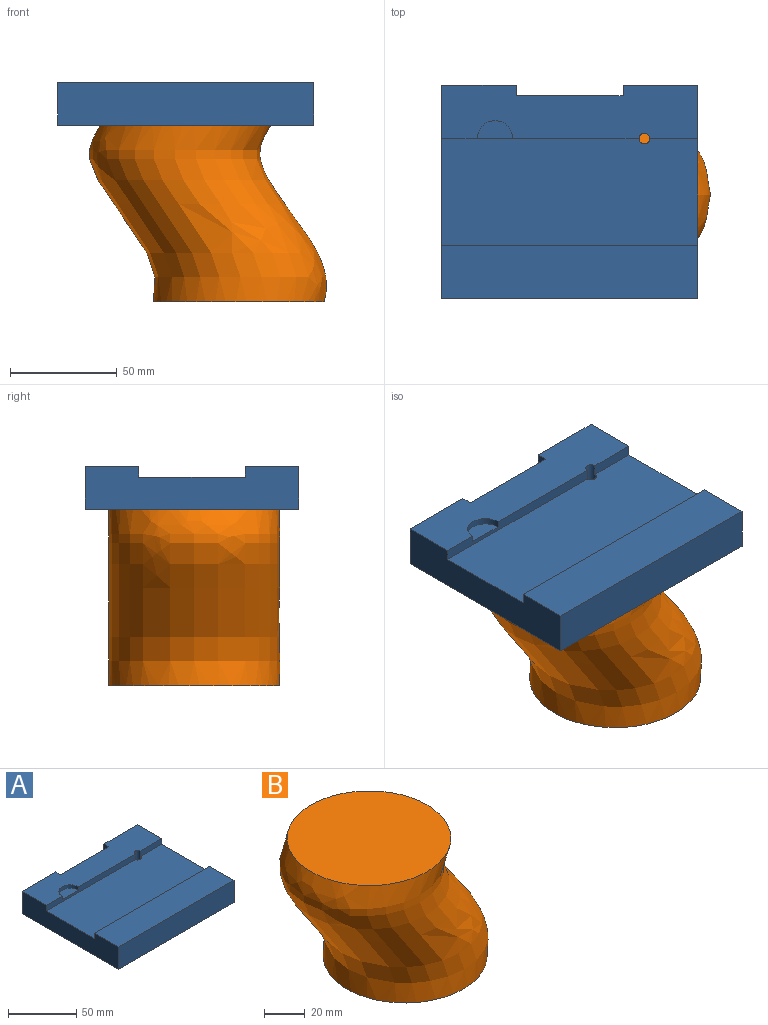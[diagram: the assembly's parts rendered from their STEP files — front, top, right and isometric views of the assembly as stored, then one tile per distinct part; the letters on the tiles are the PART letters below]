
ASSEMBLY  parts=2 mates=1
PART A: 18 faces, bbox 120x100x20 mm
  f0: plane 100x20mm, normal (-1,0,0), area 1750mm2, adj f2,f7,f8,f10,f11,f15,f16,f17
  f1: plane 100x20mm, normal (1,0,0), area 1750mm2, adj f2,f3,f8,f10,f11,f14,f15,f16
  f2: plane 120x25mm, normal (0,0,1), area 3000mm2, adj f0,f1,f8,f16
  f3: plane 35x20mm, normal (0,1,0), area 700mm2, adj f1,f4,f10,f11
  f4: plane 20x5mm, normal (-1,0,0), area 100mm2, adj f3,f5,f10,f11
  f5: plane 50x20mm, normal (0,1,0), area 1000mm2, adj f4,f6,f10,f11
  f6: plane 20x5mm, normal (1,0,0), area 100mm2, adj f5,f7,f10,f11
  f7: plane 35x20mm, normal (0,1,0), area 700mm2, adj f0,f6,f10,f11
  f8: plane 120x20mm, normal (0,-1,0), area 2400mm2, adj f0,f1,f2,f11
  f9: cylinder r=2.5mm len=20mm, axis (0,0,-1), area 274.9mm2, adj f10,f11,f14,f15,f17
  f10: plane 120x25mm, normal (0,0,1), area 2631.1mm2, adj f0,f1,f3,f4,f5,f6,f7,f9
  f11: plane 120x100mm, normal (0,0,-1), area 11730.4mm2, adj f0,f1,f3,f4,f5,f6,f7,f8
  f12: cylinder r=8.33mm len=16.67mm, axis (0,0,1), area 78.5mm2, adj f10,f13,f17
  f13: plane 16.67x8.33mm, normal (0,0,1), area 109.1mm2, adj f12,f17
  f14: plane 22.5x5mm, normal (0,-1,0), area 112.5mm2, adj f1,f9,f10,f15
  f15: plane 120x50mm, normal (0,0,1), area 5990.2mm2, adj f0,f1,f9,f14,f16,f17
  f16: plane 120x5mm, normal (0,1,0), area 600mm2, adj f0,f1,f2,f15
  f17: plane 92.5x5mm, normal (0,-1,0), area 412.5mm2, adj f0,f9,f10,f12,f13,f15
PART B: 3 faces, bbox 113.3x160x82.6 mm
  f0: plane 80x80mm, normal (0,0,-1), area 5026.5mm2, adj f2
  f1: plane 80x80mm, normal (0,0,1), area 5026.5mm2, adj f2
  f2: bspline ~160x113.28mm, area 22033.2mm2, adj f0,f1
PLACE A t=(4.83,0.76,-3.05)mm
PLACE B t=(29.67,-0.3,-95.68)mm
MATE fastened B.f1 <-> A.f11  axis (0,0,1) through (4.77,-0.3,-13.05)mm
